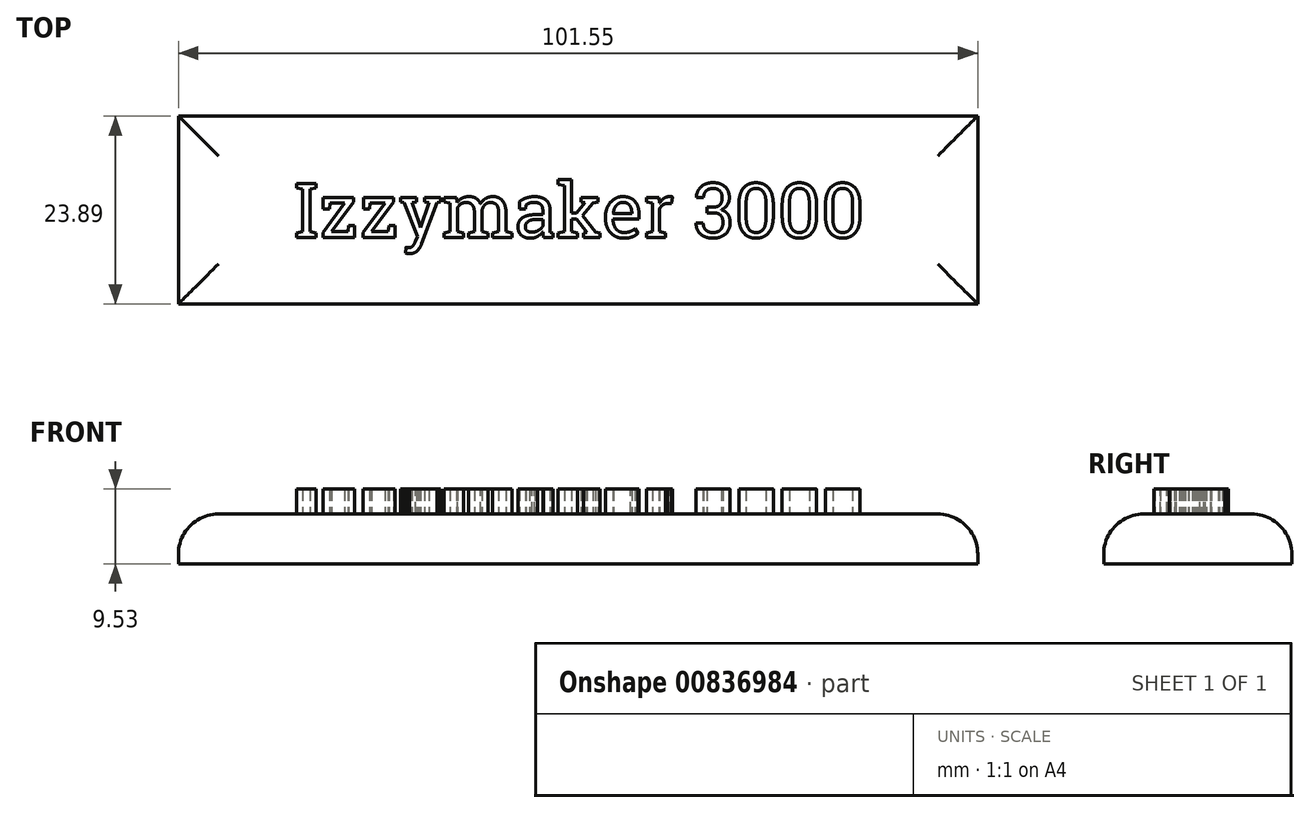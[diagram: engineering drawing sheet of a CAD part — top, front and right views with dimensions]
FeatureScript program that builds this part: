
annotation { "Feature Type Name" : "Feature", "Feature Type Description" : "" }
export const myFeature = defineFeature(function(context is Context, id is Id, definition is map)
    precondition{}
    {
        {
            var Q0;
            Q0=qCreatedBy(makeId("Top.planeOp"),FACE);
            var sketch = newSketch(context, id + "F0", { "sketchPlane" : qUnion([Q0])});
            skLineSegment(sketch, "E0.bottom", {"start": v(-46.06, -15.4) * mm, "end": v(55.49, -15.4) * mm});
            skLineSegment(sketch, "E0.top", {"start": v(-46.06, 8.49) * mm, "end": v(55.49, 8.49) * mm});
            skLineSegment(sketch, "E0.left", {"start": v(-46.06, -15.4) * mm, "end": v(-46.06, 8.49) * mm});
            skLineSegment(sketch, "E0.right", {"start": v(55.49, -15.4) * mm, "end": v(55.49, 8.49) * mm});
            skSolve(sketch);
        }
        {
            var Q0;
            Q0 = qSketchRegion(id + "F0", true);
            extrude(context, id + "F1", {"entities" : qUnion([Q0]), "depth" : 6.35 * mm, "offsetDistance" : 25.4 * mm});
        }
        {
            var Q0;
            Q0=makeQuery(id+"F1.opExtrude","CAP_FACE",FACE,{"disambiguationData":[OSD([sQuery(id+"F0.wireOp",EDGE,"E0.bottom"),sQuery(id+"F0.wireOp",EDGE,"E0.top"),sQuery(id+"F0.wireOp",EDGE,"E0.left"),sQuery(id+"F0.wireOp",EDGE,"E0.right")])],"isStart":false});
            var sketch = newSketch(context, id + "F2", { "sketchPlane" : qUnion([Q0])});
            skText(sketch, "E1", { "text": "Izzymaker 3000", "fontName": "RobotoSlab-Regular.ttf"});
            const initialGuessF2  = {"E1": [-0.03135, -0.00695, 1, 0, 0.00695]};
            skSetInitialGuess(sketch, initialGuessF2);
            skSolve(sketch);
        }
        {
            var Q0;
            Q0 = qSketchRegion(id + "F2", true);
            extrude(context, id + "F3", {"entities" : qUnion([Q0]), "operationType" : NewBodyOperationType.ADD, "depth" : 3.17 * mm, "offsetDistance" : 25.4 * mm});
        }
        {
            var Q0;
            Q0=makeQuery(id+"F1.opExtrude","CAP_EDGE",EDGE,{"disambiguationData":[OSD([sQuery(id+"F0.wireOp",EDGE,"E0.left")])],"isStart":false});
            var Q1;
            Q1=makeQuery(id+"F1.opExtrude","CAP_EDGE",EDGE,{"disambiguationData":[OSD([sQuery(id+"F0.wireOp",EDGE,"E0.top")])],"isStart":false});
            var Q2;
            Q2=makeQuery(id+"F1.opExtrude","CAP_EDGE",EDGE,{"disambiguationData":[OSD([sQuery(id+"F0.wireOp",EDGE,"E0.right")])],"isStart":false});
            var Q3;
            Q3=makeQuery(id+"F1.opExtrude","CAP_EDGE",EDGE,{"disambiguationData":[OSD([sQuery(id+"F0.wireOp",EDGE,"E0.bottom")])],"isStart":false});
            fillet(context, id + "F4", {"entities" : qUnion([Q0, Q1, Q2, Q3]), "radius" : 5.08 * mm, "tangentPropagation" : true, "allowEdgeOverflow" : false});
        }
    });
